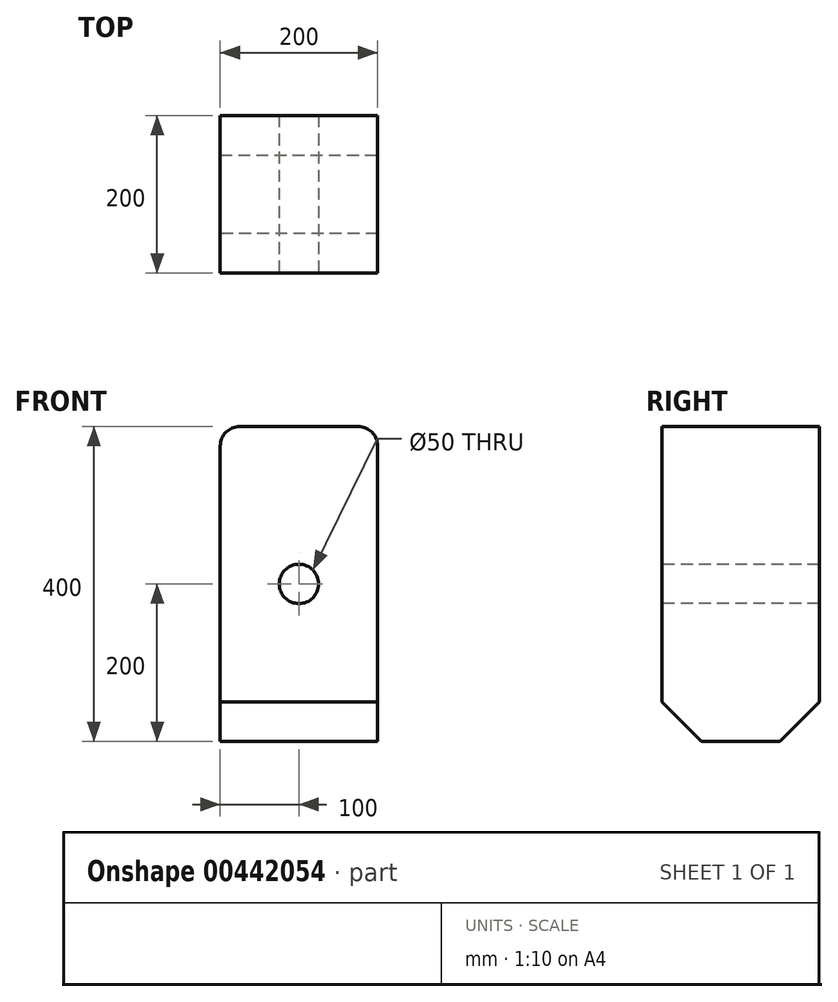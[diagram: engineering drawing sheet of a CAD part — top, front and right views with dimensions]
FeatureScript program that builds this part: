
annotation { "Feature Type Name" : "Feature", "Feature Type Description" : "" }
export const myFeature = defineFeature(function(context is Context, id is Id, definition is map)
    precondition{}
    {
        {
            var Q0;
            Q0=qCreatedBy(makeId("Front.planeOp"),FACE);
            var sketch = newSketch(context, id + "F0", { "sketchPlane" : qUnion([Q0])});
            skLineSegment(sketch, "E0.bottom", {"start": v(100, 200) * mm, "end": v(-100, 200) * mm});
            skLineSegment(sketch, "E0.top", {"start": v(100, -200) * mm, "end": v(-100, -200) * mm});
            skLineSegment(sketch, "E0.left", {"start": v(100, 200) * mm, "end": v(100, -200) * mm});
            skLineSegment(sketch, "E0.right", {"start": v(-100, 200) * mm, "end": v(-100, -200) * mm});
            skPoint(sketch, "E0.middle", {"position": v(0, 0) * mm});
            skSolve(sketch);
        }
        {
            var Q0;
            Q0=makeQuery(id+"F0.imprint","IMPRINT",FACE,{"disambiguationData":[TD([[makeQuery(id+"F0.imprint","IMPRINT",EDGE,{"derivedFrom":sQuery(id+"F0.wireOp",EDGE,"E0.bottom")}),1.0]])]});
            extrude(context, id + "F1", {"entities" : qUnion([Q0]), "depth" : 200 * mm});
        }
        {
            var Q0;
            Q0=makeQuery(id+"F1.opExtrude","CAP_FACE",FACE,{"disambiguationData":[OSD([sQuery(id+"F0.wireOp",EDGE,"E0.bottom"),sQuery(id+"F0.wireOp",EDGE,"E0.top"),sQuery(id+"F0.wireOp",EDGE,"E0.left"),sQuery(id+"F0.wireOp",EDGE,"E0.right")])],"isStart":false});
            var sketch = newSketch(context, id + "F2", { "sketchPlane" : qUnion([Q0])});
            skCircle(sketch, "E1", {"center": v(0, 0) * mm, "radius": 25 * mm});
            skSolve(sketch);
        }
        {
            var Q0;
            Q0=makeQuery(id+"F2.imprint","IMPRINT",FACE,{"disambiguationData":[TD([[makeQuery(id+"F2.imprint","IMPRINT",EDGE,{"derivedFrom":sQuery(id+"F2.wireOp",EDGE,"E1")}),1.0]])]});
            extrude(context, id + "F3", {"entities" : qUnion([Q0]), "operationType" : NewBodyOperationType.REMOVE, "endBound" : BoundingType.THROUGH_ALL, "oppositeDirection" : true, "depth" : 25 * mm});
        }
        {
            var Q0;
            Q0=makeQuery(id+"F1.opExtrude","SWEPT_EDGE",EDGE,{"disambiguationData":[OSD([sQuery(id+"F0.wireOp",EDGE,"E0.bottom"),sQuery(id+"F0.wireOp",EDGE,"E0.left")])]});
            var Q1;
            Q1=makeQuery(id+"F1.opExtrude","SWEPT_EDGE",EDGE,{"disambiguationData":[OSD([sQuery(id+"F0.wireOp",EDGE,"E0.bottom"),sQuery(id+"F0.wireOp",EDGE,"E0.right")])]});
            fillet(context, id + "F4", {"entities" : qUnion([Q0, Q1]), "radius" : 25 * mm, "tangentPropagation" : true, "allowEdgeOverflow" : false});
        }
        {
            var Q0;
            Q0=makeQuery(id+"F1.opExtrude","CAP_EDGE",EDGE,{"disambiguationData":[OSD([sQuery(id+"F0.wireOp",EDGE,"E0.top")])],"isStart":true});
            var Q1;
            Q1=makeQuery(id+"F1.opExtrude","CAP_EDGE",EDGE,{"disambiguationData":[OSD([sQuery(id+"F0.wireOp",EDGE,"E0.top")])],"isStart":false});
            chamfer(context, id + "F5", {"entities" : qUnion([Q0, Q1]), "width" : 50 * mm, "tangentPropagation" : true});
        }
    });
